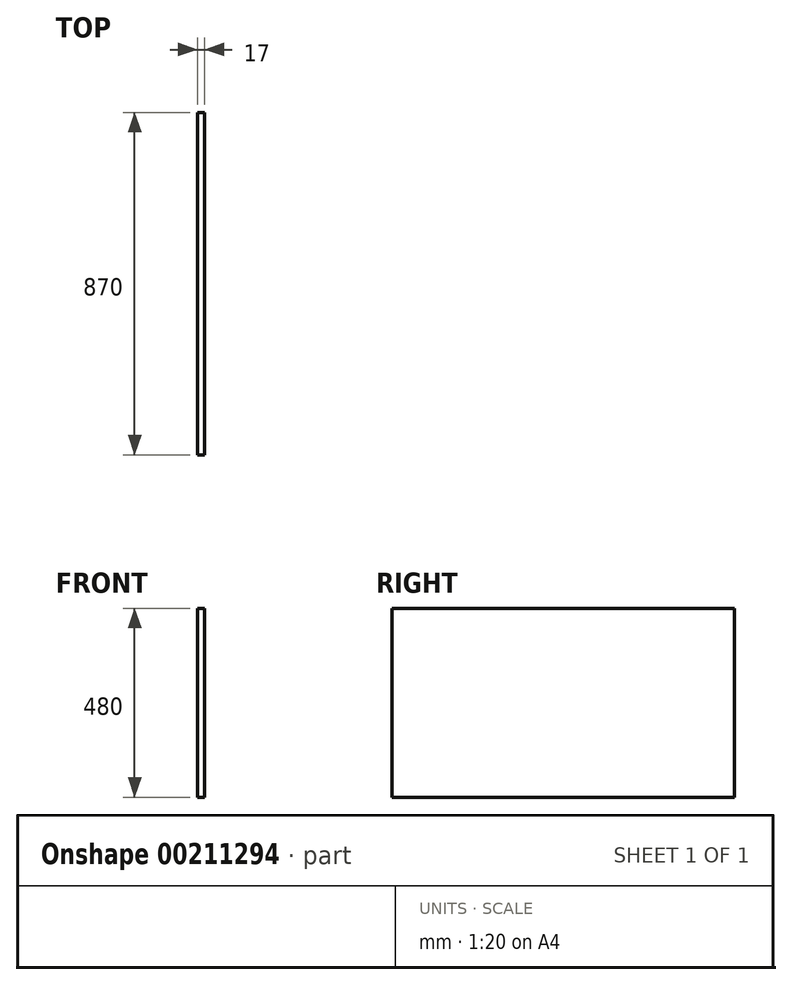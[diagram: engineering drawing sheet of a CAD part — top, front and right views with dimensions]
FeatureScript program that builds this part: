
annotation { "Feature Type Name" : "Feature", "Feature Type Description" : "" }
export const myFeature = defineFeature(function(context is Context, id is Id, definition is map)
    precondition{}
    {
        {
            var Q0;
            Q0=qCreatedBy(makeId("Top.planeOp"),FACE);
            var sketch = newSketch(context, id + "F0", { "sketchPlane" : qUnion([Q0])});
            skLineSegment(sketch, "E0.bottom", {"start": v(-16.88, 883.92) * mm, "end": v(0.12, 883.92) * mm});
            skLineSegment(sketch, "E0.top", {"start": v(-16.88, 13.92) * mm, "end": v(0.12, 13.92) * mm});
            skLineSegment(sketch, "E0.left", {"start": v(-16.88, 883.92) * mm, "end": v(-16.88, 13.92) * mm});
            skLineSegment(sketch, "E0.right", {"start": v(0.12, 883.92) * mm, "end": v(0.12, 13.92) * mm});
            skSolve(sketch);
        }
        {
            var Q0;
            Q0=makeQuery(id+"F0.imprint","IMPRINT",FACE,{"disambiguationData":[TD([[makeQuery(id+"F0.imprint","IMPRINT",EDGE,{"derivedFrom":sQuery(id+"F0.wireOp",EDGE,"E0.bottom")}),-1.0]])]});
            extrude(context, id + "F1", {"entities" : qUnion([Q0]), "depth" : 480 * mm});
        }
    });
